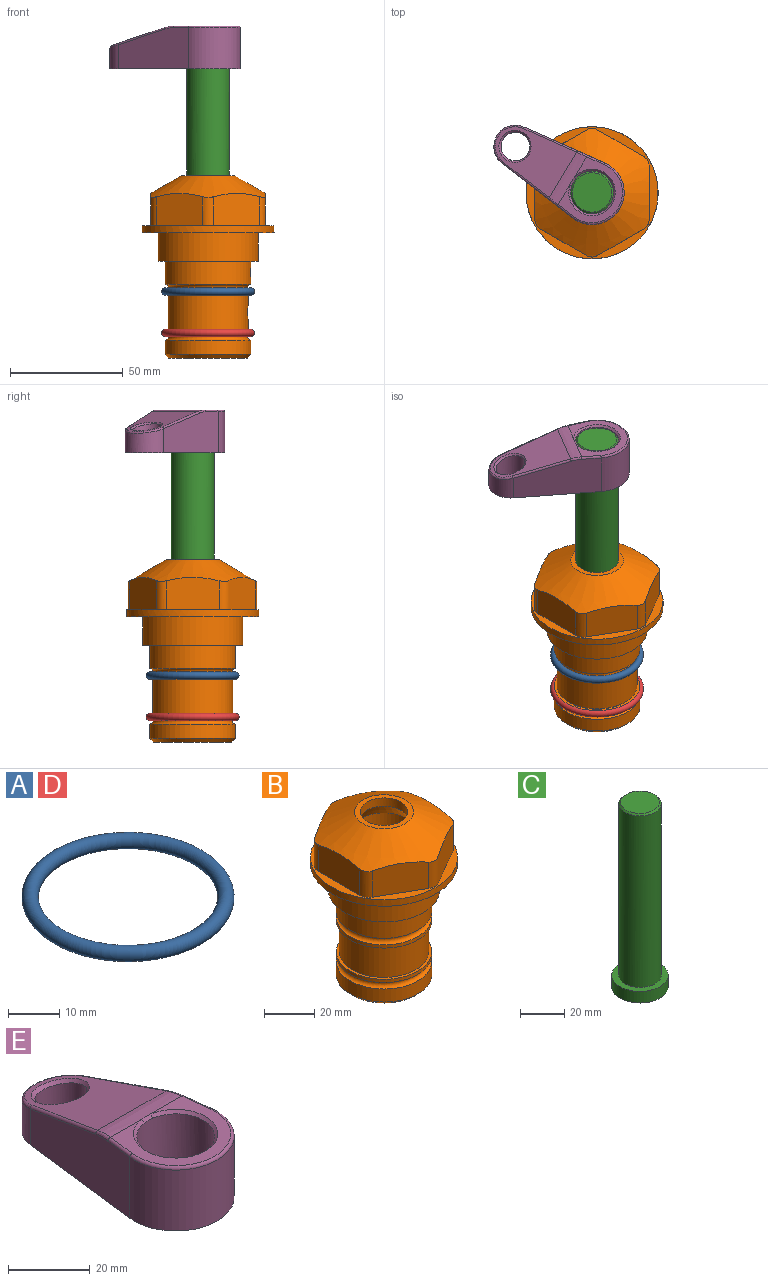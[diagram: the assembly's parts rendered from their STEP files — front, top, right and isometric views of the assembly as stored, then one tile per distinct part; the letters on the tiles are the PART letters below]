
ASSEMBLY  parts=5 mates=4
PART A: 1 faces, bbox 44.7x44.7x3.2 mm
  f0: torus R=19.05mm, axis (0,0,1), area 1193.9mm2
PART B: 36 faces, bbox 58.7x58.7x81 mm
  f0: cylinder r=17.78mm len=35.56mm, axis (0,0,1), area 1670.8mm2, adj f23,f24,f31
  f1: cylinder r=19.05mm len=38.1mm, axis (0,0,1), area 1191.9mm2, adj f26,f27,f30
  f2: plane 58.66x58.66mm, normal (0,0,-1), area 1150.6mm2, adj f3,f28
  f3: cylinder r=29.33mm len=58.66mm, axis (0,0,-1), area 585.1mm2, adj f2,f4
  f4: plane 58.66x58.66mm, normal (0,0,1), area 475.9mm2, adj f3,f5,f6,f7,f8,f9,f10,f11
  f5: plane 20.32x14.34mm, normal (-0.5,0.87,0), area 324.4mm2, adj f4,f15,f16,f17
  f6: plane 20.32x14.34mm, normal (0.5,0.87,0), area 324.4mm2, adj f4,f14,f15,f17
  f7: plane 23.48x14.34mm, normal (1,0,0), area 324.4mm2, adj f4,f13,f14,f17
  f8: plane 20.32x14.34mm, normal (0.5,-0.87,0), area 324.4mm2, adj f4,f12,f13,f17
  f9: plane 20.32x14.34mm, normal (-0.5,-0.87,0), area 324.4mm2, adj f4,f11,f12,f17
  f10: plane 23.48x14.34mm, normal (-1,0,0), area 324.4mm2, adj f4,f11,f16,f17
  f11: cylinder r=5.08mm len=12.85mm, axis (0,0,-1), area 67.2mm2, adj f4,f9,f10,f17
  f12: cylinder r=5.08mm len=12.85mm, axis (0,0,-1), area 67.2mm2, adj f4,f8,f9,f17
  f13: cylinder r=5.08mm len=12.85mm, axis (0,0,-1), area 67.2mm2, adj f4,f7,f8,f17
  f14: cylinder r=5.08mm len=12.85mm, axis (0,0,-1), area 67.2mm2, adj f4,f6,f7,f17
  f15: cylinder r=5.08mm len=12.85mm, axis (0,0,-1), area 67.2mm2, adj f4,f5,f6,f17
  f16: cylinder r=5.08mm len=12.85mm, axis (0,0,-1), area 67.2mm2, adj f4,f5,f10,f17
  f17: cone r=11.73mm half-angle=60deg, axis (0,0,-1), area 2071.8mm2, adj f5,f6,f7,f8,f9,f10,f11,f12
  f18: plane 23.46x23.46mm, normal (0,0,1), area 147.4mm2, adj f17,f35
  f19: plane 34.93x34.93mm, normal (0,0,-1), area 958mm2, adj f29
  f20: cylinder r=19.05mm len=38.1mm, axis (0,0,1), area 760.1mm2, adj f21,f29
  f21: torus R=19.05mm, axis (0,0,1), area 565.3mm2, adj f20,f22
  f22: cylinder r=19.05mm len=38.1mm, axis (0,0,1), area 190mm2, adj f21,f23
  f23: plane 38.1x38.1mm, normal (0,0,1), area 146.9mm2, adj f0,f22
  f24: plane 38.1x38.1mm, normal (0,0,-1), area 146.9mm2, adj f0,f25
  f25: cylinder r=19.05mm len=38.1mm, axis (0,0,1), area 190mm2, adj f24,f26
  f26: torus R=19.05mm, axis (0,0,1), area 565.3mm2, adj f1,f25
  f27: plane 44.45x44.45mm, normal (0,0,-1), area 411.7mm2, adj f1,f28
  f28: cylinder r=22.23mm len=44.45mm, axis (0,0,1), area 1773.5mm2, adj f2,f27
  f29: cone r=19.05mm half-angle=45deg, axis (0,0,1), area 257.5mm2, adj f19,f20
  f30: cylinder r=3.17mm len=6.75mm, axis (-1,0,0), area 128mm2, adj f1,f33
  f31: cylinder r=3.17mm len=6.35mm, axis (-1,0,0), area 102.5mm2, adj f0,f33
  f32: plane 25.4x25.4mm, normal (0,0,1), area 506.7mm2, adj f33
  f33: cylinder r=12.7mm len=66.42mm, axis (0,0,-1), area 5236.2mm2, adj f30,f31,f32,f34
  f34: cone r=9.53mm half-angle=30deg, axis (0,0,-1), area 443.4mm2, adj f33,f35
  f35: cylinder r=9.53mm len=19.05mm, axis (0,0,-1), area 240.9mm2, adj f18,f34
PART C: 6 faces, bbox 25.4x25.4x101.6 mm
  f0: plane 17.46x17.46mm, normal (0,0,1), area 239.5mm2, adj f5
  f1: plane 25.4x25.4mm, normal (0,0,-1), area 506.7mm2, adj f2
  f2: cylinder r=12.7mm len=25.4mm, axis (0,0,1), area 506.7mm2, adj f1,f3
  f3: plane 25.4x25.4mm, normal (0,0,1), area 221.7mm2, adj f2,f4
  f4: cylinder r=9.53mm len=94.46mm, axis (0,0,1), area 5653mm2, adj f3,f5
  f5: cone r=8.73mm half-angle=45deg, axis (0,0,-1), area 64.4mm2, adj f0,f4
PART D: same geometry as A
PART E: 31 faces, bbox 31.7x65.5x19.8 mm
  f0: plane 39.12x18.26mm, normal (0.99,0.12,0), area 612.2mm2, adj f1,f4,f7,f11,f13,f15
  f1: cylinder r=9.53mm len=18.91mm, axis (0,0,-1), area 296.1mm2, adj f0,f2,f7,f17
  f2: plane 39.12x18.26mm, normal (-0.99,0.12,0), area 612.2mm2, adj f1,f4,f7,f12,f14,f16
  f3: cylinder r=6.35mm len=12.7mm, axis (0,0,-1), area 362.4mm2, adj f7,f18
  f4: cylinder r=14.29mm len=28.58mm, axis (0,0,-1), area 882.2mm2, adj f0,f2,f7,f10
  f5: cylinder r=9.53mm len=19.05mm, axis (0,0,-1), area 1092.6mm2, adj f7,f19,f20
  f6: plane 26.99x23.69mm, normal (0,0,1), area 216.2mm2, adj f9,f10,f11,f12,f19
  f7: plane 63.5x28.58mm, normal (0,0,-1), area 661.8mm2, adj f0,f1,f2,f3,f4,f5,f22,f23
  f8: plane 33.52x23.6mm, normal (0,0.26,0.97), area 486mm2, adj f9,f15,f16,f17,f18
  f9: cylinder r=19.05mm len=24.72mm, axis (1,0,0), area 120.4mm2, adj f6,f8,f13,f14,f20
  f10: torus R=13.49mm, axis (0,0,1), area 59mm2, adj f4,f6,f11,f12
  f11: cylinder r=0.79mm len=8.67mm, axis (0.12,-0.99,0), area 10.8mm2, adj f0,f6,f10,f13
  f12: cylinder r=0.79mm len=8.67mm, axis (0.12,0.99,0), area 10.8mm2, adj f2,f6,f10,f14
  f13: bspline ~4.95x1.42mm, area 6.1mm2, adj f0,f9,f11,f15
  f14: bspline ~4.95x1.42mm, area 6.1mm2, adj f2,f9,f12,f16
  f15: cylinder r=0.79mm len=25.95mm, axis (0.12,-0.96,0.26), area 32.9mm2, adj f0,f8,f13,f17
  f16: cylinder r=0.79mm len=25.95mm, axis (0.12,0.96,-0.26), area 32.9mm2, adj f2,f8,f14,f17
  f17: bspline ~18.91x8.38mm, area 30mm2, adj f1,f8,f15,f16
  f18: bspline ~14.29x14.29mm, area 48.3mm2, adj f3,f8
  f19: cone r=9.53mm half-angle=45deg, axis (0,0,1), area 66.5mm2, adj f5,f6,f20
  f20: bspline ~3.22x0.96mm, area 3.5mm2, adj f5,f9,f19
  f21: plane 2.75x2.72mm, normal (0,0,-1), area 2.9mm2, adj f23,f25,f28
  f22: plane 23.05x15.88mm, normal (-0.99,-0.12,0), area 323.6mm2, adj f7,f25,f26,f27,f28,f29
  f23: plane 23.05x15.88mm, normal (0.99,-0.12,0), area 323.6mm2, adj f7,f21,f25,f27,f28,f30
  f24: cylinder r=9.53mm len=10.69mm, axis (0,0,-1), area 114.7mm2, adj f7,f27,f29,f30
  f25: cylinder r=12.7mm len=20.59mm, axis (0,0,-1), area 381.1mm2, adj f7,f21,f22,f23,f26,f28
  f26: plane 2.75x2.72mm, normal (0,0,-1), area 2.9mm2, adj f22,f25,f28
  f27: plane 19.72x18.37mm, normal (0,-0.26,-0.97), area 291.8mm2, adj f22,f23,f24,f28,f29,f30
  f28: cylinder r=15.88mm len=19.92mm, axis (1,0,0), area 54.8mm2, adj f21,f22,f23,f25,f26,f27
  f29: cylinder r=1.59mm len=11mm, axis (0,0,-1), area 34.7mm2, adj f7,f22,f24,f27
  f30: cylinder r=1.59mm len=11mm, axis (0,0,-1), area 34.7mm2, adj f7,f23,f24,f27
PLACE A t=(0,0,-1.59)mm
PLACE B at identity fixed
PLACE C rot(axis=(0,0,1),59.1deg) t=(0,0,27.55)mm
PLACE D t=(0,0,-20)mm
PLACE E rot(axis=(0,0,1),59.1deg) t=(0,0,28.35)mm
MATE cylindrical C.f2 <-> B.f0  axis (0,0,-1) through (0,0,-10.55)mm
MATE fastened C.f2 <-> E.f4  axis (0,0,1) through (0,0,91.05)mm
MATE fastened A.f0 <-> B.f0  axis (0,0,1) through (0,0,-26.1)mm
MATE fastened D.f0 <-> B.f0  axis (0,0,1) through (0,0,-44.51)mm
